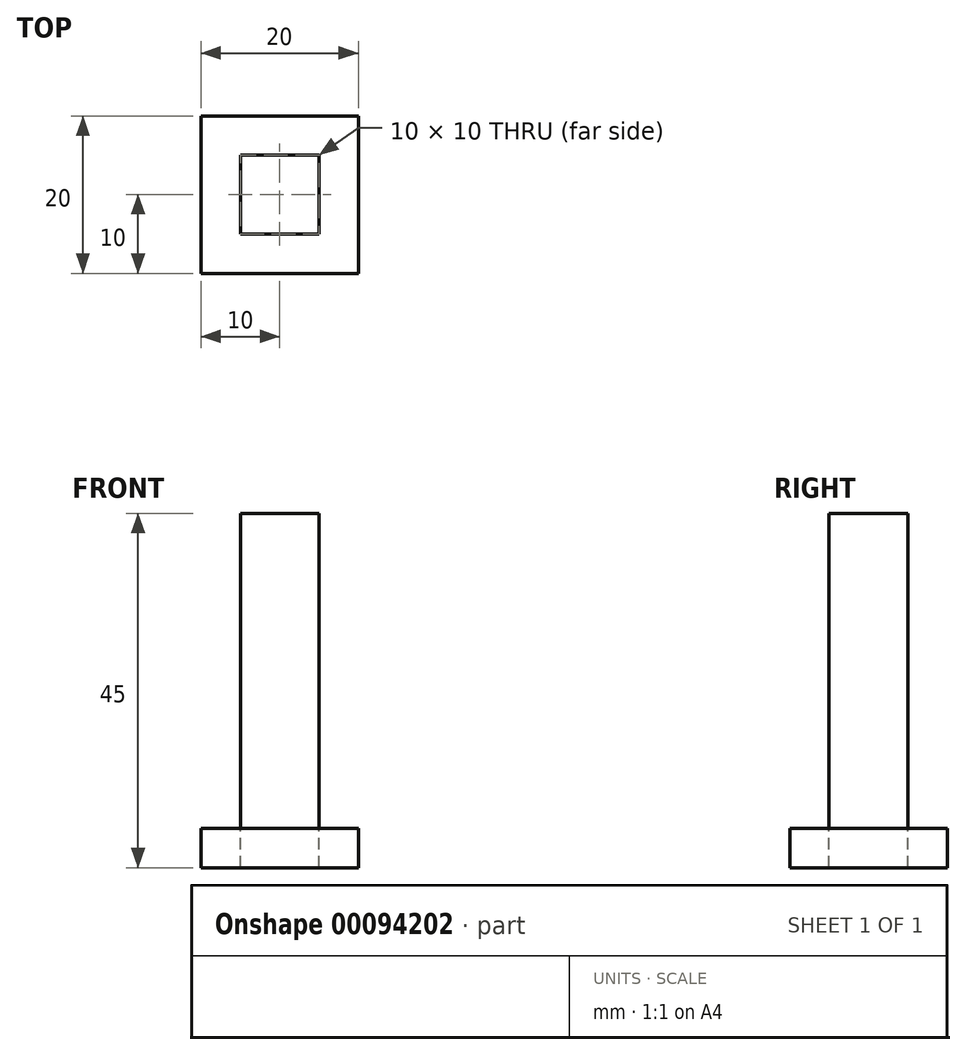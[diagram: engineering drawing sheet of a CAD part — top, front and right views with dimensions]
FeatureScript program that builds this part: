
annotation { "Feature Type Name" : "Feature", "Feature Type Description" : "" }
export const myFeature = defineFeature(function(context is Context, id is Id, definition is map)
    precondition{}
    {
        {
            var Q0;
            Q0=qCreatedBy(makeId("Top.planeOp"),FACE);
            var sketch = newSketch(context, id + "F0", { "sketchPlane" : qUnion([Q0])});
            skLineSegment(sketch, "E0.bottom", {"start": v(5, -5) * mm, "end": v(-5, -5) * mm});
            skLineSegment(sketch, "E0.top", {"start": v(5, 5) * mm, "end": v(-5, 5) * mm});
            skLineSegment(sketch, "E0.left", {"start": v(5, -5) * mm, "end": v(5, 5) * mm});
            skLineSegment(sketch, "E0.right", {"start": v(-5, -5) * mm, "end": v(-5, 5) * mm});
            skPoint(sketch, "E0.middle", {"position": v(0, 0) * mm});
            skSolve(sketch);
        }
        {
            var Q0;
            Q0=makeQuery(id+"F0.imprint","IMPRINT",FACE,{"disambiguationData":[TD([[makeQuery(id+"F0.imprint","IMPRINT",EDGE,{"derivedFrom":sQuery(id+"F0.wireOp",EDGE,"E0.bottom")}),-1.0]])]});
            extrude(context, id + "F1", {"entities" : qUnion([Q0]), "depth" : 40 * mm});
        }
        {
            var Q0;
            Q0=makeQuery(id+"F0.imprint","IMPRINT",FACE,{"disambiguationData":[TD([[makeQuery(id+"F0.imprint","IMPRINT",EDGE,{"derivedFrom":sQuery(id+"F0.wireOp",EDGE,"E0.bottom")}),-1.0]])]});
            var sketch = newSketch(context, id + "F2", { "sketchPlane" : qUnion([Q0])});
            skLineSegment(sketch, "E1.bottom", {"start": v(10, -10) * mm, "end": v(-10, -10) * mm});
            skLineSegment(sketch, "E1.top", {"start": v(10, 10) * mm, "end": v(-10, 10) * mm});
            skLineSegment(sketch, "E1.left", {"start": v(10, -10) * mm, "end": v(10, 10) * mm});
            skLineSegment(sketch, "E1.right", {"start": v(-10, -10) * mm, "end": v(-10, 10) * mm});
            skPoint(sketch, "E1.middle", {"position": v(0, 0) * mm});
            skSolve(sketch);
        }
        {
            var Q0;
            Q0=makeQuery(id+"F2.imprint","IMPRINT",FACE,{"disambiguationData":[TD([[makeQuery(id+"F2.imprint","IMPRINT",EDGE,{"derivedFrom":sQuery(id+"F2.wireOp",EDGE,"E1.bottom")}),-1.0]])]});
            extrude(context, id + "F3", {"entities" : qUnion([Q0]), "oppositeDirection" : true, "depth" : 5 * mm});
        }
    });
